# Revit family: Bathtub-American_Standard-Evolution-2645V_Series
name_source: partatom
category: Plumbing Fixtures
revit_build: Autodesk Revit 2014 (Build: 20130308_1515(x64)
units: mm (PartAtom-declared; Revit-internal decimal feet)

## types (9) — shared parameters
Assembly Code = D2010510
CW Connection = Yes
CWFU = 3
Default Elevation = 0"
Description = Evolution 66 Inch by 36 Inch Oval Bathtub
HW Connection = Yes
HWFU = 3
Height = 19 3/4"
Installation Type = Deck Mounted
Length = 66"
Manufacturer = American Standard
Price = Prices may vary. Please consult Manufacturer Representative for most up-to-date price list.
Product Documentation Link = https://www.americanstandard-us.com
Product Page URL = https://www.americanstandard-us.com
URL = http://www.americanstandard-us.com
Vent Connection = No
WFU = 4
Warranty Information = 1 Year Limited
Waste Connection = Yes
Waste Connection Diameter = 1 1/2"
Waste Connection Radius = 3/4"
Width = 36"

## per-type parameters (varying)
| type | EverClean | Finish | Material | Water Jets |
| 2645.V.011 | No | Acrylic-American Standard-011-Arctic | Acrylic-American Standard-011-Arctic | Yes |
| 2645.V.020 | No | Acrylic-American Standard-020-White | Acrylic-American Standard-020-White | Yes |
| 2645.V.222 | No | Acrylic-American Standard-222-Linen | Acrylic-American Standard-020-White | Yes |
| 2645.V002.011 | No | Acrylic-American Standard-011-Arctic | Acrylic-American Standard-011-Arctic | No |
| 2645.V002.020 | No | Acrylic-American Standard-020-White | Acrylic-American Standard-020-White | No |
| 2645.V002.222 | No | Acrylic-American Standard-222-Linen | Acrylic-American Standard-222-Linen | No |
| 2645.VC.011 | Yes | Acrylic-American Standard-011-Arctic | Acrylic-American Standard-011-Arctic | Yes |
| 2645.VC.020 | Yes | Acrylic-American Standard-020-White | Acrylic-American Standard-020-White | Yes |
| 2645.VC.222 | Yes | Acrylic-American Standard-222-Linen | Acrylic-American Standard-222-Linen | Yes |

note: column(s) folded — value = type name in every type: Model

## geometry (parser evidence)
native form markers: Sweep x1
no freeform markers — native parametric forms only
